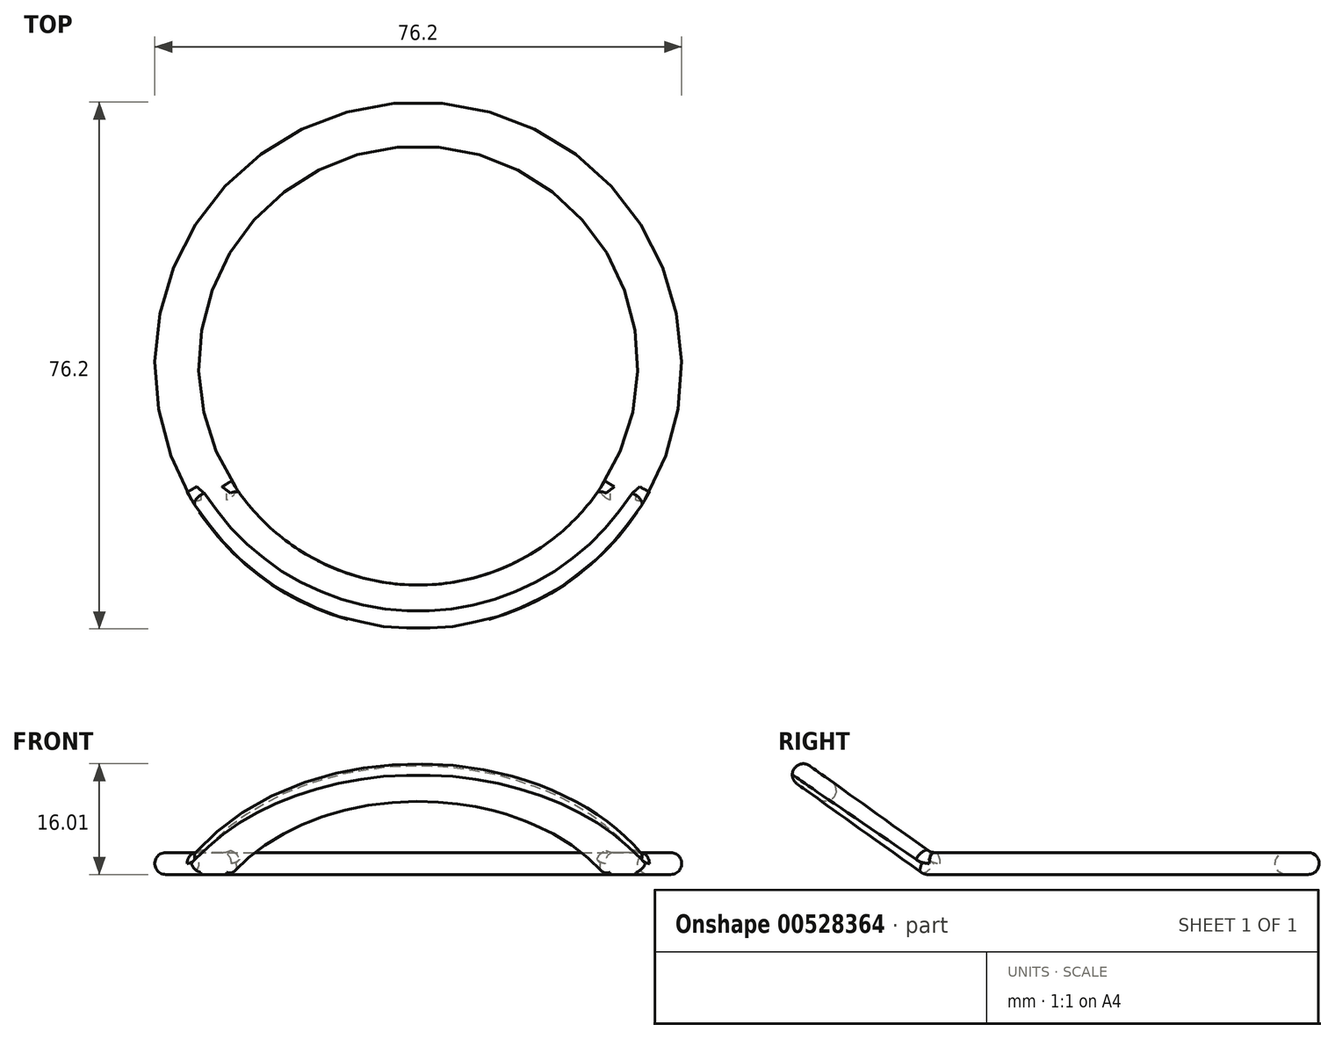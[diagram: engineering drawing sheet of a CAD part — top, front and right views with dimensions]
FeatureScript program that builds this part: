
annotation { "Feature Type Name" : "Feature", "Feature Type Description" : "" }
export const myFeature = defineFeature(function(context is Context, id is Id, definition is map)
    precondition{}
    {
        {
            var Q0;
            Q0=qCreatedBy(makeId("Right.planeOp"),FACE);
            var sketch = newSketch(context, id + "F0", { "sketchPlane" : qUnion([Q0])});
            skLineSegment(sketch, "E0", {"start": v(57.15, 0) * mm, "end": v(0, 0) * mm});
            skLineSegment(sketch, "E1", {"start": v(0, 0) * mm, "end": v(-44.45, 31.75) * mm});
            skLineSegment(sketch, "E2.0", {"start": v(1.02, 3.18) * mm, "end": v(-42.6, 34.33) * mm});
            skLineSegment(sketch, "E2.1", {"start": v(57.15, 3.18) * mm, "end": v(1.02, 3.17) * mm});
            skLineSegment(sketch, "E3", {"start": v(-44.45, 31.75) * mm, "end": v(-42.6, 34.33) * mm});
            skLineSegment(sketch, "E4", {"start": v(57.15, 0) * mm, "end": v(57.15, 3.18) * mm});
            skSolve(sketch);
        }
        {
            var Q0;
            Q0=makeQuery(id+"F0.imprint","IMPRINT",FACE,{"disambiguationData":[TD([[makeQuery(id+"F0.imprint","IMPRINT",EDGE,{"derivedFrom":sQuery(id+"F0.wireOp",EDGE,"E0")}),-1.0]])]});
            extrude(context, id + "F1", {"entities" : qUnion([Q0]), "depth" : 44.45 * mm, "offsetDistance" : 25.4 * mm, "hasSecondDirection" : true, "secondDirectionOppositeDirection" : true, "secondDirectionDepth" : 44.45 * mm});
        }
        {
            var Q0;
            Q0=qCreatedBy(makeId("Top.planeOp"),FACE);
            var sketch = newSketch(context, id + "F2", { "sketchPlane" : qUnion([Q0])});
            skCircle(sketch, "E5", {"center": v(0, 19.05) * mm, "radius": 38.1 * mm});
            skCircle(sketch, "E6", {"center": v(0, 19.05) * mm, "radius": 31.75 * mm});
            skSolve(sketch);
        }
        {
            var Q0;
            Q0 = qSketchRegion(id + "F2", true);
            extrude(context, id + "F3", {"entities" : qUnion([Q0]), "operationType" : NewBodyOperationType.INTERSECT, "depth" : 28.45 * mm, "offsetDistance" : 25.4 * mm});
        }
        {
            var Q0;
            Q0=makeQuery(id+"F1.opExtrude","SWEPT_FACE",FACE,{"disambiguationData":[OSD([sQuery(id+"F0.wireOp",EDGE,"E2.0")])]});
            var Q1;
            Q1=makeQuery(id+"F1.opExtrude","SWEPT_FACE",FACE,{"disambiguationData":[OSD([sQuery(id+"F0.wireOp",EDGE,"E2.1")])]});
            var Q2;
            Q2=makeQuery(id+"F1.opExtrude","SWEPT_FACE",FACE,{"disambiguationData":[OSD([sQuery(id+"F0.wireOp",EDGE,"E1")])]});
            var Q3;
            Q3=makeQuery(id+"F1.opExtrude","SWEPT_FACE",FACE,{"disambiguationData":[OSD([sQuery(id+"F0.wireOp",EDGE,"E0")])]});
            fillet(context, id + "F4", {"entities" : qUnion([Q0, Q1, Q2, Q3]), "radius" : 1.59 * mm, "tangentPropagation" : true, "allowEdgeOverflow" : false});
        }
    });
